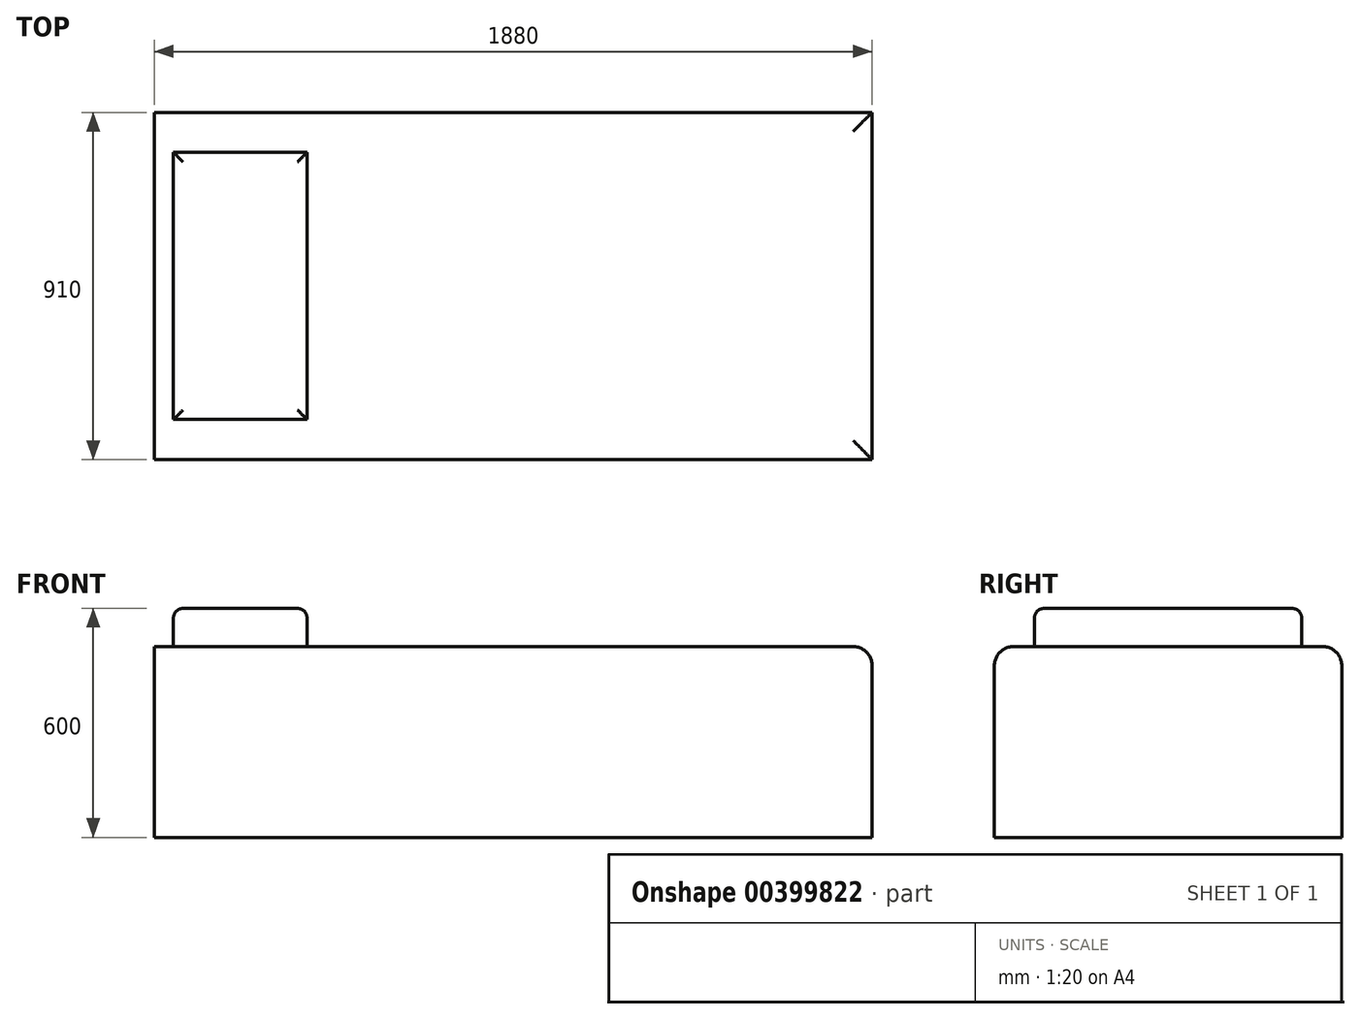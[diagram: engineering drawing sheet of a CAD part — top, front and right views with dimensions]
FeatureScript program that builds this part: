
annotation { "Feature Type Name" : "Feature", "Feature Type Description" : "" }
export const myFeature = defineFeature(function(context is Context, id is Id, definition is map)
    precondition{}
    {
        {
            var Q0;
            Q0=qCreatedBy(makeId("Top.planeOp"),FACE);
            var sketch = newSketch(context, id + "F0", { "sketchPlane" : qUnion([Q0])});
            skLineSegment(sketch, "E0.bottom", {"start": v(0, 0) * mm, "end": v(1880, 0) * mm});
            skLineSegment(sketch, "E0.top", {"start": v(0, 910) * mm, "end": v(1880, 910) * mm});
            skLineSegment(sketch, "E0.left", {"start": v(0, 0) * mm, "end": v(0, 910) * mm});
            skLineSegment(sketch, "E0.right", {"start": v(1880, 0) * mm, "end": v(1880, 910) * mm});
            skSolve(sketch);
        }
        {
            var Q0;
            Q0 = qSketchRegion(id + "F0", true);
            extrude(context, id + "F1", {"entities" : qUnion([Q0]), "depth" : 500 * mm});
        }
        {
            var Q0;
            Q0=makeQuery(id+"F1.opExtrude","CAP_FACE",FACE,{"disambiguationData":[OSD([sQuery(id+"F0.wireOp",EDGE,"E0.bottom"),sQuery(id+"F0.wireOp",EDGE,"E0.top"),sQuery(id+"F0.wireOp",EDGE,"E0.left"),sQuery(id+"F0.wireOp",EDGE,"E0.right")])],"isStart":false});
            var sketch = newSketch(context, id + "F2", { "sketchPlane" : qUnion([Q0])});
            skLineSegment(sketch, "E1.bottom", {"start": v(50, 105) * mm, "end": v(400, 105) * mm});
            skLineSegment(sketch, "E1.top", {"start": v(50, 805) * mm, "end": v(400, 805) * mm});
            skLineSegment(sketch, "E1.left", {"start": v(50, 105) * mm, "end": v(50, 805) * mm});
            skLineSegment(sketch, "E1.right", {"start": v(400, 105) * mm, "end": v(400, 805) * mm});
            skLineSegment(sketch, "E2", {"start": v(50, 805) * mm, "end": v(50, 910) * mm, "construction": true});
            skLineSegment(sketch, "E3", {"start": v(50, 105) * mm, "end": v(50, 0) * mm, "construction": true});
            skSolve(sketch);
        }
        {
            var Q0;
            Q0 = qSketchRegion(id + "F2", true);
            extrude(context, id + "F3", {"entities" : qUnion([Q0]), "operationType" : NewBodyOperationType.ADD, "depth" : 100 * mm});
        }
        {
            var Q0;
            Q0=makeQuery(id+"F3.opExtrude","CAP_EDGE",EDGE,{"disambiguationData":[OSD([sQuery(id+"F2.wireOp",EDGE,"E1.left")])],"isStart":false});
            var Q1;
            Q1=makeQuery(id+"F3.opExtrude","CAP_FACE",FACE,{"disambiguationData":[OSD([sQuery(id+"F2.wireOp",EDGE,"E1.bottom"),sQuery(id+"F2.wireOp",EDGE,"E1.top"),sQuery(id+"F2.wireOp",EDGE,"E1.left"),sQuery(id+"F2.wireOp",EDGE,"E1.right")])],"isStart":false});
            fillet(context, id + "F4", {"entities" : qUnion([Q0, Q1]), "radius" : 25 * mm, "tangentPropagation" : true, "allowEdgeOverflow" : false});
        }
        {
            var Q0;
            Q0=makeQuery(id+"F1.opExtrude","CAP_EDGE",EDGE,{"disambiguationData":[OSD([sQuery(id+"F0.wireOp",EDGE,"E0.top")])],"isStart":false});
            var Q1;
            Q1=makeQuery(id+"F1.opExtrude","CAP_EDGE",EDGE,{"disambiguationData":[OSD([sQuery(id+"F0.wireOp",EDGE,"E0.right")])],"isStart":false});
            var Q2;
            Q2=makeQuery(id+"F1.opExtrude","CAP_EDGE",EDGE,{"disambiguationData":[OSD([sQuery(id+"F0.wireOp",EDGE,"E0.bottom")])],"isStart":false});
            fillet(context, id + "F5", {"entities" : qUnion([Q0, Q1, Q2]), "radius" : 50 * mm, "tangentPropagation" : true, "allowEdgeOverflow" : false});
        }
    });
